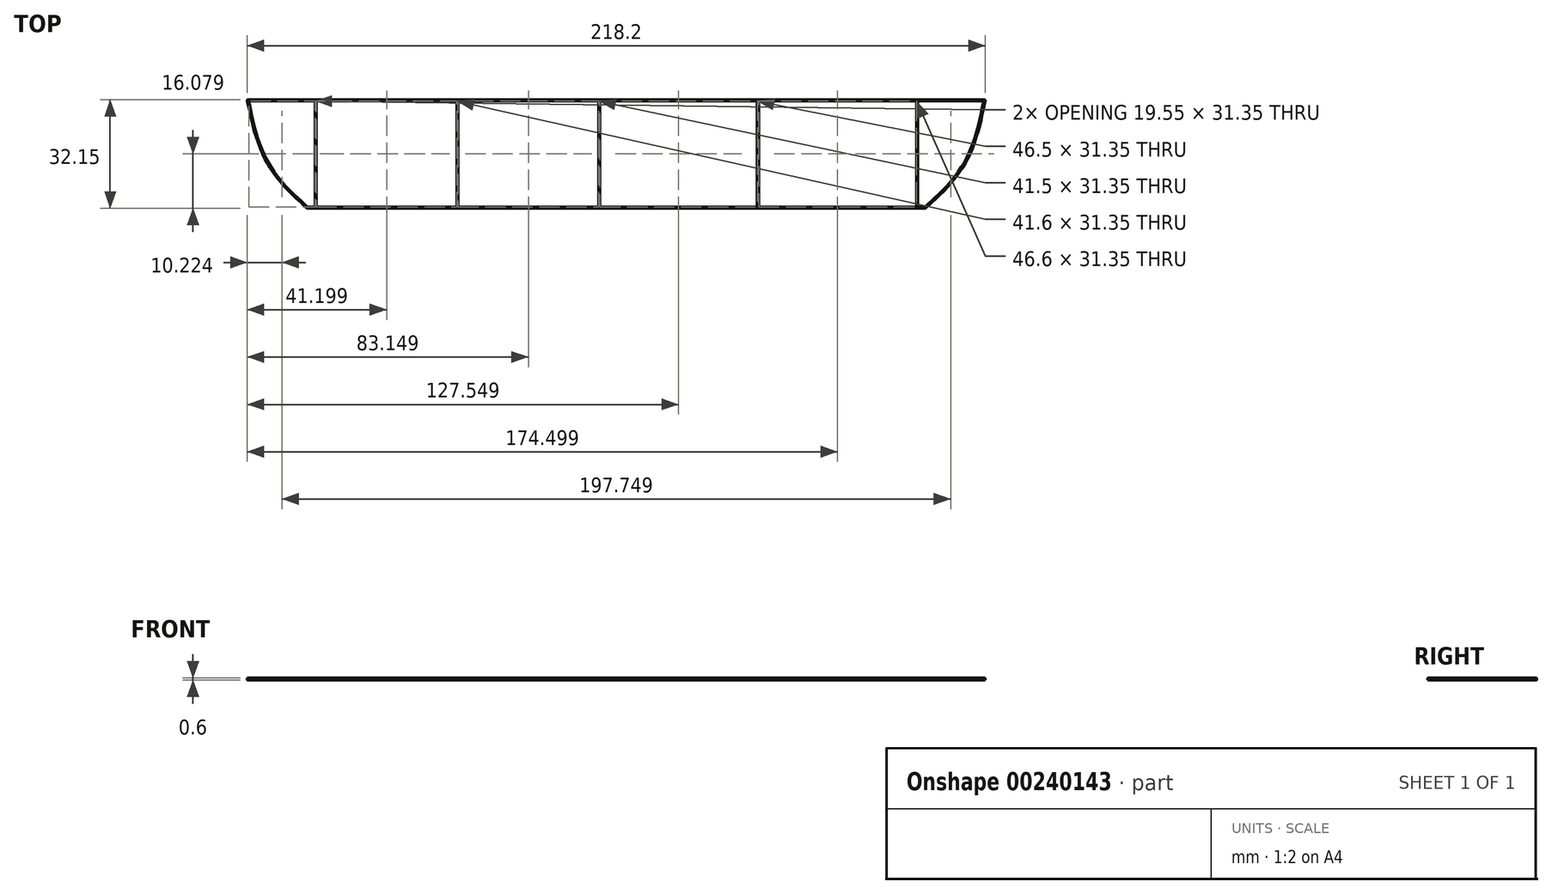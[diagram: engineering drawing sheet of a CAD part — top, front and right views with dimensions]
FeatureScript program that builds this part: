
annotation { "Feature Type Name" : "Feature", "Feature Type Description" : "" }
export const myFeature = defineFeature(function(context is Context, id is Id, definition is map)
    precondition{}
    {
        {
            var Q0;
            Q0=qCreatedBy(makeId("Top.planeOp"),FACE);
            var sketch = newSketch(context, id + "F0", { "sketchPlane" : qUnion([Q0])});
            skLineSegment(sketch, "E0", {"start": v(-10.28, -29.54) * mm, "end": v(-10.28, 31.69) * mm, "construction": true});
            skPoint(sketch, "E1.MirrorCS.end.orphan", {"position": v(-101.68, -29.54) * mm});
            skPoint(sketch, "E1.MirrorCS.start.orphan", {"position": v(-119.18, 2.21) * mm});
            skArc(sketch, "E2.0.startCap", {"start": v(98.62, 2.41) * mm, "mid": v(98.77, 2.34) * mm, "end": v(98.81, 2.17) * mm});
            skArc(sketch, "E2.0.endCap", {"start": v(81.26, -29.68) * mm, "mid": v(81.2, -29.72) * mm, "end": v(81.12, -29.74) * mm});
            skFitSpline(sketch, "E2.0.left", {"points": [v(98.81, 2.17) * mm, v(98.11, -1) * mm, v(97.06, -5.77) * mm, v(95.09, -11.75) * mm, v(93.19, -15.95) * mm, v(90.71, -19.75) * mm, v(86.83, -24.4) * mm, v(83.48, -27.57) * mm, v(81.26, -29.68) * mm]});
            skFitSpline(sketch, "E2.0.right", {"points": [v(98.42, 2.26) * mm, v(97.72, -0.92) * mm, v(96.67, -5.67) * mm, v(94.71, -11.6) * mm, v(92.84, -15.76) * mm, v(90.4, -19.5) * mm, v(86.54, -24.12) * mm, v(83.2, -27.28) * mm, v(80.98, -29.4) * mm]});
            skLineSegment(sketch, "E2.1.left", {"start": v(78.82, -29.34) * mm, "end": v(81.04, -29.34) * mm});
            skLineSegment(sketch, "E2.1.right", {"start": v(78.62, -29.74) * mm, "end": v(81.12, -29.74) * mm});
            skArc(sketch, "E2.2.endCap", {"start": v(-119.38, 2.17) * mm, "mid": v(-119.34, 2.34) * mm, "end": v(-119.18, 2.41) * mm});
            skLineSegment(sketch, "E2.2.left", {"start": v(-99.38, 2.01) * mm, "end": v(-118.93, 2.01) * mm});
            skLineSegment(sketch, "E2.2.right", {"start": v(-99.18, 2.41) * mm, "end": v(-119.18, 2.41) * mm});
            skArc(sketch, "E2.3.startCap", {"start": v(-119.38, 2.17) * mm, "mid": v(-119.34, 2.34) * mm, "end": v(-119.18, 2.41) * mm});
            skFitSpline(sketch, "E2.3.right", {"points": [v(-119.38, 2.17) * mm, v(-118.68, -1) * mm, v(-117.62, -5.77) * mm, v(-115.65, -11.75) * mm, v(-113.75, -15.95) * mm, v(-111.27, -19.75) * mm, v(-107.39, -24.4) * mm, v(-104.04, -27.57) * mm, v(-101.82, -29.68) * mm]});
            skArc(sketch, "E2.4.endCap", {"start": v(-10.48, 31.69) * mm, "mid": v(-10.28, 31.89) * mm, "end": v(-10.08, 31.69) * mm});
            skLineSegment(sketch, "E2.5.left", {"start": v(-56.98, 2.01) * mm, "end": v(-56.98, -29.34) * mm});
            skLineSegment(sketch, "E2.5.right", {"start": v(-57.38, 2.01) * mm, "end": v(-57.38, -29.34) * mm});
            skLineSegment(sketch, "E2.6.left", {"start": v(-15.08, 2.01) * mm, "end": v(-15.08, -29.34) * mm});
            skLineSegment(sketch, "E2.6.right", {"start": v(-15.48, 2.01) * mm, "end": v(-15.48, -29.34) * mm});
            skLineSegment(sketch, "E2.7.left", {"start": v(78.62, -29.74) * mm, "end": v(-99.18, -29.74) * mm});
            skLineSegment(sketch, "E2.7.right", {"start": v(78.42, -29.34) * mm, "end": v(31.82, -29.34) * mm});
            skLineSegment(sketch, "E2.8.left", {"start": v(78.82, 2.01) * mm, "end": v(78.82, -29.34) * mm});
            skLineSegment(sketch, "E2.8.right", {"start": v(78.42, 2.01) * mm, "end": v(78.42, -29.34) * mm});
            skArc(sketch, "E2.9.endCap", {"start": v(98.62, 2.41) * mm, "mid": v(98.77, 2.34) * mm, "end": v(98.81, 2.17) * mm});
            skLineSegment(sketch, "E2.9.left", {"start": v(78.62, 2.41) * mm, "end": v(98.62, 2.41) * mm});
            skLineSegment(sketch, "E2.9.right", {"start": v(78.82, 2.01) * mm, "end": v(98.37, 2.01) * mm});
            skArc(sketch, "E2.10.endCap", {"start": v(-101.68, -29.74) * mm, "mid": v(-101.76, -29.72) * mm, "end": v(-101.82, -29.68) * mm});
            skLineSegment(sketch, "E2.10.left", {"start": v(-99.18, -29.74) * mm, "end": v(-101.68, -29.74) * mm});
            skLineSegment(sketch, "E2.10.right", {"start": v(-99.38, -29.34) * mm, "end": v(-101.6, -29.34) * mm});
            skLineSegment(sketch, "E2.11.left", {"start": v(31.82, 2.01) * mm, "end": v(31.82, -29.34) * mm});
            skLineSegment(sketch, "E2.11.right", {"start": v(31.42, 2.01) * mm, "end": v(31.42, -29.34) * mm});
            skLineSegment(sketch, "E2.12.left", {"start": v(-99.18, 2.41) * mm, "end": v(78.62, 2.41) * mm});
            skLineSegment(sketch, "E2.12.right", {"start": v(-98.98, 2.01) * mm, "end": v(-57.38, 2.01) * mm});
            skLineSegment(sketch, "E2.13.left", {"start": v(-98.98, 2.01) * mm, "end": v(-98.98, -29.34) * mm});
            skLineSegment(sketch, "E2.13.right", {"start": v(-99.38, 2.01) * mm, "end": v(-99.38, -29.34) * mm});
            skPoint(sketch, "E3.orphan", {"position": v(31.62, 2.21) * mm});
            skLineSegment(sketch, "E4.trimOffspring", {"start": v(31.82, 2.01) * mm, "end": v(78.42, 2.01) * mm});
            skLineSegment(sketch, "E5.trimOffspring", {"start": v(-15.08, 2.01) * mm, "end": v(31.42, 2.01) * mm});
            skLineSegment(sketch, "E6.trimOffspring", {"start": v(-56.98, 2.01) * mm, "end": v(-15.48, 2.01) * mm});
            skPoint(sketch, "E2.5.startCap.center.orphan", {"position": v(-57.18, 2.21) * mm});
            skPoint(sketch, "E2.2.startCap.center.orphan", {"position": v(-99.18, 2.21) * mm});
            skFitSpline(sketch, "E7.trimOffspring", {"points": [v(-118.99, 2.26) * mm, v(-118.28, -0.92) * mm, v(-117.23, -5.67) * mm, v(-115.28, -11.6) * mm, v(-113.4, -15.76) * mm, v(-110.95, -19.5) * mm, v(-107.1, -24.12) * mm, v(-103.77, -27.28) * mm, v(-101.54, -29.4) * mm]});
            skLineSegment(sketch, "E8.trimOffspring", {"start": v(-57.38, -29.34) * mm, "end": v(-98.98, -29.34) * mm});
            skLineSegment(sketch, "E9.trimOffspring", {"start": v(-15.48, -29.34) * mm, "end": v(-56.98, -29.34) * mm});
            skPoint(sketch, "E10.orphan", {"position": v(-15.28, -29.54) * mm});
            skLineSegment(sketch, "E11.trimOffspring", {"start": v(31.42, -29.34) * mm, "end": v(-15.08, -29.34) * mm});
            skPoint(sketch, "E12.trimOffspring.end.orphan", {"position": v(-99.18, -29.54) * mm});
            skPoint(sketch, "E13.end.orphan", {"position": v(78.62, -29.54) * mm});
            skPoint(sketch, "E14.trimOffspring.end.orphan", {"position": v(78.62, 2.21) * mm});
            skSolve(sketch);
        }
        {
            var Q0;
            Q0=makeQuery(id+"F0.imprint","IMPRINT",FACE,{"disambiguationData":[TD([[makeQuery(id+"F0.imprint","IMPRINT",EDGE,{"derivedFrom":sQuery(id+"F0.wireOp",EDGE,"E2.0.left")}),-1.0]])]});
            extrude(context, id + "F1", {"entities" : qUnion([Q0]), "depth" : .6 * mm});
        }
    });
